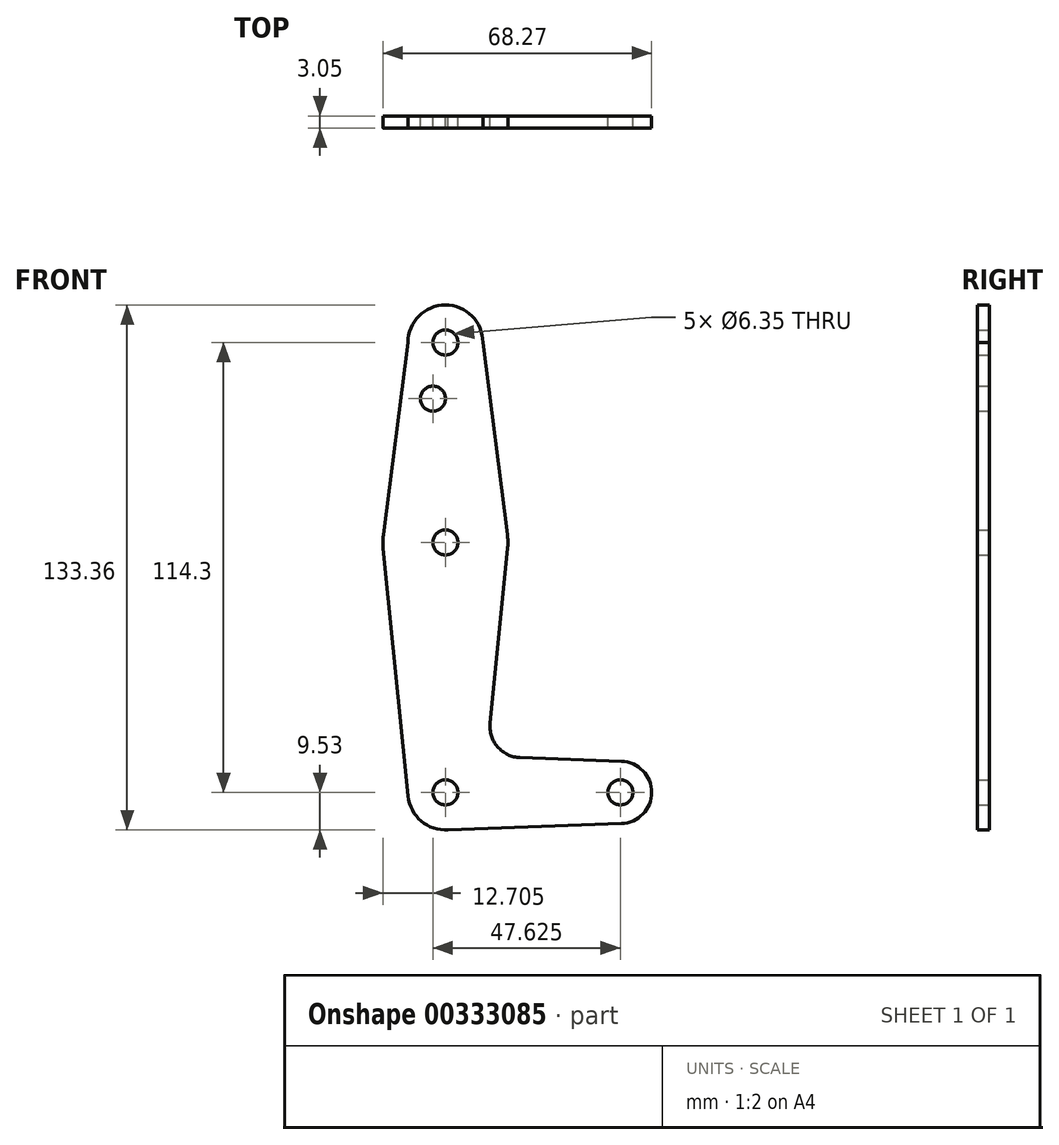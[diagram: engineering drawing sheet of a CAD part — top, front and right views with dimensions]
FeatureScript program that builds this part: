
annotation { "Feature Type Name" : "Feature", "Feature Type Description" : "" }
export const myFeature = defineFeature(function(context is Context, id is Id, definition is map)
    precondition{}
    {
        {
            var Q0;
            Q0=qCreatedBy(makeId("Front.planeOp"),FACE);
            var sketch = newSketch(context, id + "F0", { "sketchPlane" : qUnion([Q0])});
            skLineSegment(sketch, "E0", {"start": v(0, 0) * mm, "end": v(0, 114.3) * mm, "construction": true});
            skLineSegment(sketch, "E1", {"start": v(0, 0) * mm, "end": v(44.45, 0) * mm, "construction": true});
            skCircle(sketch, "E2", {"center": v(0, 0) * mm, "radius": 9.53 * mm});
            skCircle(sketch, "E3", {"center": v(44.45, 0) * mm, "radius": 7.94 * mm});
            skCircle(sketch, "E4", {"center": v(0, 114.3) * mm, "radius": 9.52 * mm});
            skCircle(sketch, "E5", {"center": v(0, 63.5) * mm, "radius": 15.88 * mm});
            skLineSegment(sketch, "E6", {"start": v(-9.52, 114.3) * mm, "end": v(-15.75, 65.5) * mm});
            skLineSegment(sketch, "E7", {"start": v(9.52, 114.3) * mm, "end": v(15.75, 65.5) * mm});
            skLineSegment(sketch, "E8", {"start": v(18.97, 8.85) * mm, "end": v(44.73, 7.93) * mm});
            skLineSegment(sketch, "E9", {"start": v(0, -9.53) * mm, "end": v(44.73, -7.93) * mm});
            skCircle(sketch, "E10", {"center": v(0, 114.3) * mm, "radius": 3.18 * mm});
            skCircle(sketch, "E11", {"center": v(0, 63.5) * mm, "radius": 3.18 * mm});
            skCircle(sketch, "E12", {"center": v(-3.18, 100.03) * mm, "radius": 3.18 * mm});
            skCircle(sketch, "E13", {"center": v(0, 0) * mm, "radius": 3.18 * mm});
            skCircle(sketch, "E14", {"center": v(44.45, 0) * mm, "radius": 3.18 * mm});
            skLineSegment(sketch, "E15", {"start": v(15.8, 61.91) * mm, "end": v(11.34, 17.59) * mm});
            skLineSegment(sketch, "E16", {"start": v(-9.48, -0.95) * mm, "end": v(-15.8, 61.91) * mm});
            skArc(sketch, "E17.filletArc", {"start": v(11.34, 17.59) * mm, "mid": v(13.26, 11.57) * mm, "end": v(18.97, 8.85) * mm});
            skSolve(sketch);
        }
        {
            var Q0;
            Q0 = qSketchRegion(id + "F0", true);
            extrude(context, id + "F1", {"entities" : qUnion([Q0]), "depth" : 3.05 * mm});
        }
    });
